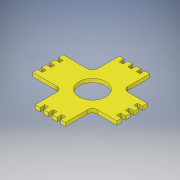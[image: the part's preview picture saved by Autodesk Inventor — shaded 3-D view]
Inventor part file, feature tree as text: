
AUTODESK INVENTOR PART (.ipt)
format: ipt  version: 2019.1 (Build 231200000, 200)  size: 239,616 bytes
history: native  units: in
note: dims shown in document units (in); Inventor stores cm internally (conversion verified against a paired STEP export)
features: extrude x1, sketch x1
ambient origin geometry x8: Origin, YZ Plane, XZ Plane, XY Plane, X Axis, Y Axis, Z Axis, Center Point
bodies: Body1 (feature_tree)
feature tree (2):
  extrude  "Extrusion3"  Depth=0.0591in
  sketch  "Sketch2"  dims[d5=7.3819in d6=4.9213in d7=4.9213in d8=7.3819in d15=1.378in d16=0.4921in d17=0.4921in d18=0.4429in d19=1.378in d20=0.4429in d21=0.4429in d25=0.0591in d26=0.0591in d27=0.0591in d28=0.0787in d29=0.0787in d30=0.0787in d31=0.0787in d43=0.0787in d44=0.0787in d45=0.0787in d46=0.0787in d47=0.0787in d48=0.0787in d49=0.0787in d50=0.0787in d51=0.0787in d52=0.0787in d53=0.0787in d60=0.0787in d61=0.0591in d62=0.0591in d63=0.0591in d64=0.0591in d65=0.0591in d66=0.0591in d67=0.0591in d68=0.0591in d69=0.0591in d70=0.0787in d71=0.0787in d72=0.0787in d74=0.0787in d75=0.0787in d76=0.0787in d77=0.0787in d78=0.0787in d79=0.0787in d80=0.0787in d81=0.4331in d82=0.4331in d83=0.4331in d84=0.4331in d85=0.0787in d86=0.0787in d87=0.0787in d88=0.0787in d89=0.3937in d90=0.3937in d91=0.4724in d92=0.4724in d97=0.0787in d98=0.0787in d99=0.0787in d100=0.315in d102=0.0787in d105=0.2461in d106=0.2461in d107=0.06in d108=0.0in d109=0.0787in d110=0.0in d111=0.0787in d112=0.0in d113=0.0787in]
